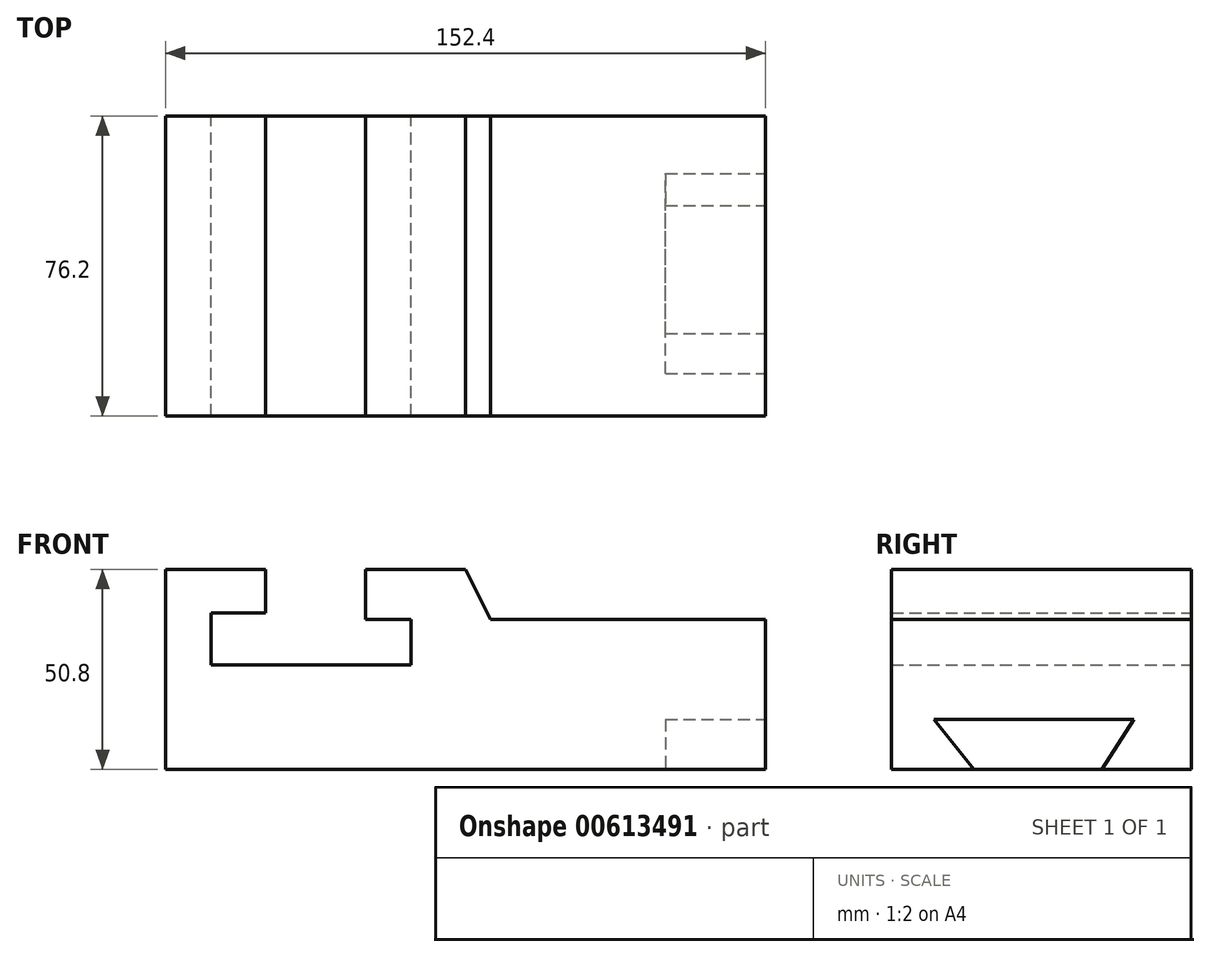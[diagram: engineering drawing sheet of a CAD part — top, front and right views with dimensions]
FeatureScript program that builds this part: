
annotation { "Feature Type Name" : "Feature", "Feature Type Description" : "" }
export const myFeature = defineFeature(function(context is Context, id is Id, definition is map)
    precondition{}
    {
        {
            var Q0;
            Q0=qCreatedBy(makeId("Front.planeOp"),FACE);
            var sketch = newSketch(context, id + "F0", { "sketchPlane" : qUnion([Q0])});
            skLineSegment(sketch, "E0", {"start": v(-53.47, -15.11) * mm, "end": v(-53.47, 35.69) * mm});
            skLineSegment(sketch, "E1", {"start": v(-53.47, -15.11) * mm, "end": v(98.93, -15.11) * mm});
            skLineSegment(sketch, "E2", {"start": v(98.93, -15.11) * mm, "end": v(98.93, 22.99) * mm});
            skLineSegment(sketch, "E3", {"start": v(98.93, 22.99) * mm, "end": v(29.08, 22.99) * mm});
            skLineSegment(sketch, "E4", {"start": v(29.08, 22.99) * mm, "end": v(22.73, 35.69) * mm});
            skLineSegment(sketch, "E5", {"start": v(22.73, 35.69) * mm, "end": v(-2.67, 35.69) * mm});
            skLineSegment(sketch, "E6", {"start": v(-2.67, 35.69) * mm, "end": v(-2.67, 22.99) * mm});
            skLineSegment(sketch, "E7", {"start": v(-2.67, 22.99) * mm, "end": v(8.84, 22.99) * mm});
            skLineSegment(sketch, "E8", {"start": v(8.84, 22.99) * mm, "end": v(8.84, 11.47) * mm});
            skLineSegment(sketch, "E9", {"start": v(-28.07, 35.69) * mm, "end": v(-53.47, 35.69) * mm});
            skLineSegment(sketch, "E10", {"start": v(-28.07, 35.69) * mm, "end": v(-28.07, 24.68) * mm});
            skLineSegment(sketch, "E11", {"start": v(-28.07, 24.68) * mm, "end": v(-41.96, 24.68) * mm});
            skLineSegment(sketch, "E12", {"start": v(-41.96, 24.68) * mm, "end": v(-41.96, 11.47) * mm});
            skLineSegment(sketch, "E13", {"start": v(-41.96, 11.47) * mm, "end": v(8.84, 11.47) * mm});
            skSolve(sketch);
        }
        {
            var Q0;
            Q0 = qSketchRegion(id + "F0", true);
            extrude(context, id + "F1", {"entities" : qUnion([Q0]), "depth" : 76.2 * mm, "offsetDistance" : 25.4 * mm});
        }
        {
            var Q0;
            Q0=makeQuery(id+"F1.opExtrude","SWEPT_FACE",FACE,{"disambiguationData":[OSD([sQuery(id+"F0.wireOp",EDGE,"E2")])]});
            var sketch = newSketch(context, id + "F2", { "sketchPlane" : qUnion([Q0])});
            skLineSegment(sketch, "E14", {"start": v(-65.4, -2.41) * mm, "end": v(-14.6, -2.41) * mm});
            skLineSegment(sketch, "E15", {"start": v(-65.4, -2.41) * mm, "end": v(-55.25, -15.11) * mm});
            skLineSegment(sketch, "E16", {"start": v(-14.6, -2.41) * mm, "end": v(-22.73, -15.11) * mm});
            skSolve(sketch);
        }
        {
            var Q0;
            Q0 = qSketchRegion(id + "F2", true);
            var Q1;
            Q1=makeQuery(id+"F2.imprint","IMPRINT",FACE,{"disambiguationData":[TD([[makeQuery(id+"F2.imprint","IMPRINT",EDGE,{"derivedFrom":sQuery(id+"F2.wireOp",EDGE,"E14")}),-1.0]])]});
            extrude(context, id + "F3", {"entities" : qUnion([Q0, Q1]), "operationType" : NewBodyOperationType.REMOVE, "oppositeDirection" : true, "depth" : 25.4 * mm, "offsetDistance" : 25.4 * mm});
        }
    });
